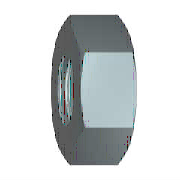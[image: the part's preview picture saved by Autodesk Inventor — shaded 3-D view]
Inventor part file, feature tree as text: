
AUTODESK INVENTOR PART (.ipt)
format: ipt  version: 2014 SP1 (Build 180222100, 222)  size: 174,592 bytes
history: native  units: mm (DEFAULTED — no unit token found)
features: sketch x3, chamfer x1, hole x1, other x1, plane x1
ambient origin geometry x7: Origin, YZ Plane, XZ Plane, X Axis, Y Axis, Z Axis, Center Point
bodies: Solid1 (feature_tree), Body (feature_tree)
feature tree (7):
  chamfer  "Chamfer1"  Distance=4.363323mm
  hole  "Thread"  [1 undecoded]
  other  "Work Axis1"
  plane  "Work Plane1"
  sketch  "Sketch1"  dims[d0=12.83161mm]
  sketch  "Sketch2"  dims[d1=5.5626mm]
  sketch  "Sketch3"  dims[d2=0.0mm d3=4.363323mm d4=4.363323mm d5=11.1125mm d6=11.1125mm d7=90.0deg d25=5.3594mm d26=6.0mm d27=4.0mm d28=2.0mm d29=14.3117mm d30=8.0mm d31=20.594885mm d8=0.491005mm d9=30.0deg d10=0.491005mm d11=30.0deg d13=0.0mm d14=0.0mm d39=0.0mm d40=0.491005mm d41=0.491005mm d42=0.0mm]
note: 1 required parameter value undecoded (feature->parameter linkage not recoverable at this tier; creation-order binding heuristic only, values carry confidence <= 0.55)
